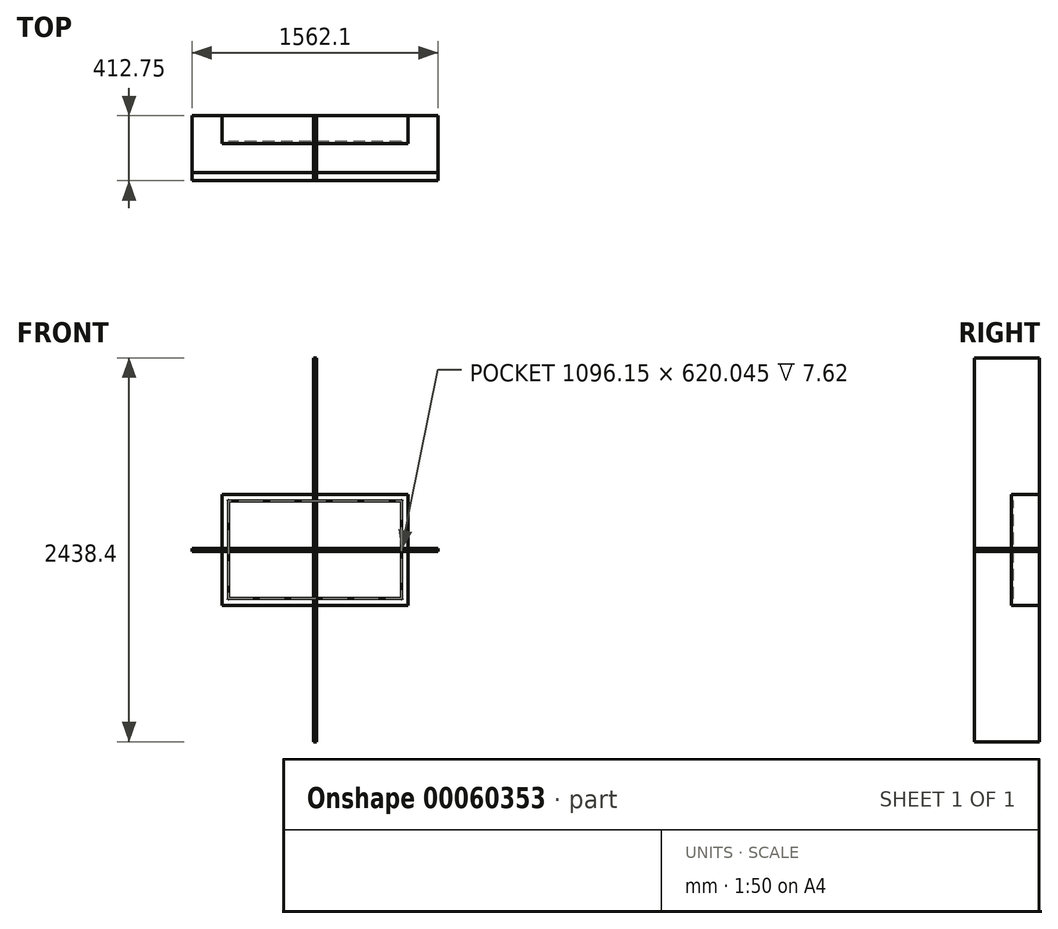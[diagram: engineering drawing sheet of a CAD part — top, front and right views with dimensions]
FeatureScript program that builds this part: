
annotation { "Feature Type Name" : "Feature", "Feature Type Description" : "" }
export const myFeature = defineFeature(function(context is Context, id is Id, definition is map)
    precondition{}
    {
        {
            var Q0;
            Q0=qCreatedBy(makeId("Front.planeOp"),FACE);
            var sketch = newSketch(context, id + "F0", { "sketchPlane" : qUnion([Q0])});
            skLineSegment(sketch, "E0.rect.bottom", {"start": v(590.55, 352.43) * mm, "end": v(-590.55, 352.43) * mm});
            skLineSegment(sketch, "E0.rect.top", {"start": v(590.55, -352.43) * mm, "end": v(-590.55, -352.43) * mm});
            skLineSegment(sketch, "E0.rect.left", {"start": v(590.55, 352.43) * mm, "end": v(590.55, -352.43) * mm});
            skLineSegment(sketch, "E0.rect.right", {"start": v(-590.55, 352.43) * mm, "end": v(-590.55, -352.43) * mm});
            skPoint(sketch, "E0.rect.middle", {"position": v(0, 0) * mm});
            skSolve(sketch);
        }
        {
            var Q0;
            Q0=makeQuery(id+"F0.imprint","IMPRINT",FACE,{"disambiguationData":[TD([[makeQuery(id+"F0.imprint","IMPRINT",EDGE,{"derivedFrom":sQuery(id+"F0.wireOp",EDGE,"E0.rect.bottom")}),1.0]])]});
            extrude(context, id + "F1", {"entities" : qUnion([Q0]), "depth" : 177.8 * mm});
        }
        {
            var Q0;
            Q0=makeQuery(id+"F1.opExtrude","CAP_FACE",FACE,{"disambiguationData":[OSD([sQuery(id+"F0.wireOp",EDGE,"E0.rect.bottom"),sQuery(id+"F0.wireOp",EDGE,"E0.rect.top"),sQuery(id+"F0.wireOp",EDGE,"E0.rect.left"),sQuery(id+"F0.wireOp",EDGE,"E0.rect.right")])],"isStart":false});
            var sketch = newSketch(context, id + "F2", { "sketchPlane" : qUnion([Q0])});
            skLineSegment(sketch, "E1.rect.bottom", {"start": v(548.08, -310.02) * mm, "end": v(-548.08, -310.02) * mm});
            skLineSegment(sketch, "E1.rect.top", {"start": v(548.08, 310.02) * mm, "end": v(-548.08, 310.02) * mm});
            skLineSegment(sketch, "E1.rect.left", {"start": v(548.08, -310.02) * mm, "end": v(548.08, 310.02) * mm});
            skLineSegment(sketch, "E1.rect.right", {"start": v(-548.08, -310.02) * mm, "end": v(-548.08, 310.02) * mm});
            skPoint(sketch, "E1.rect.middle", {"position": v(0, 0) * mm});
            skSolve(sketch);
        }
        {
            var Q0;
            Q0=qCreatedBy(makeId("Front.planeOp"),FACE);
            var sketch = newSketch(context, id + "F3", { "sketchPlane" : qUnion([Q0])});
            skLineSegment(sketch, "E2.rect.bottom", {"start": v(9.53, 1219.2) * mm, "end": v(-9.53, 1219.2) * mm});
            skLineSegment(sketch, "E2.rect.top", {"start": v(9.53, -1219.2) * mm, "end": v(-9.53, -1219.2) * mm});
            skLineSegment(sketch, "E2.rect.left", {"start": v(9.53, 1219.2) * mm, "end": v(9.53, -1219.2) * mm});
            skLineSegment(sketch, "E2.rect.right", {"start": v(-9.53, 1219.2) * mm, "end": v(-9.53, -1219.2) * mm});
            skPoint(sketch, "E2.rect.middle", {"position": v(0, 0) * mm});
            skSolve(sketch);
        }
        {
            var Q0;
            Q0=qCreatedBy(makeId("Front.planeOp"),FACE);
            var sketch = newSketch(context, id + "F4", { "sketchPlane" : qUnion([Q0])});
            skLineSegment(sketch, "E3.rect.bottom", {"start": v(781.05, 9.53) * mm, "end": v(-781.05, 9.53) * mm});
            skLineSegment(sketch, "E3.rect.top", {"start": v(781.05, -9.52) * mm, "end": v(-781.05, -9.52) * mm});
            skLineSegment(sketch, "E3.rect.left", {"start": v(781.05, 9.53) * mm, "end": v(781.05, -9.52) * mm});
            skLineSegment(sketch, "E3.rect.right", {"start": v(-781.05, 9.53) * mm, "end": v(-781.05, -9.52) * mm});
            skPoint(sketch, "E3.rect.middle", {"position": v(0, 0) * mm});
            skSolve(sketch);
        }
        {
            var Q0;
            Q0=makeQuery(id+"F4.imprint","IMPRINT",FACE,{"disambiguationData":[TD([[makeQuery(id+"F4.imprint","IMPRINT",EDGE,{"derivedFrom":sQuery(id+"F4.wireOp",EDGE,"E3.rect.bottom")}),1.0]])]});
            extrude(context, id + "F5", {"entities" : qUnion([Q0]), "depth" : 412.75 * mm});
        }
        {
            var Q0;
            Q0=makeQuery(id+"F4.imprint","IMPRINT",FACE,{"disambiguationData":[TD([[makeQuery(id+"F4.imprint","IMPRINT",EDGE,{"derivedFrom":sQuery(id+"F4.wireOp",EDGE,"E3.rect.bottom")}),1.0]])]});
            extrude(context, id + "F6", {"entities" : qUnion([Q0]), "depth" : 361.95 * mm});
        }
        {
            var Q0;
            Q0=makeQuery(id+"F4.imprint","IMPRINT",FACE,{"disambiguationData":[TD([[makeQuery(id+"F4.imprint","IMPRINT",EDGE,{"derivedFrom":sQuery(id+"F4.wireOp",EDGE,"E3.rect.bottom")}),1.0]])]});
            extrude(context, id + "F7", {"entities" : qUnion([Q0]), "depth" : 361.95 * mm});
        }
        {
            var Q0;
            Q0=makeQuery(id+"F4.imprint","IMPRINT",FACE,{"disambiguationData":[TD([[makeQuery(id+"F4.imprint","IMPRINT",EDGE,{"derivedFrom":sQuery(id+"F4.wireOp",EDGE,"E3.rect.bottom")}),1.0]])]});
            extrude(context, id + "F8", {"entities" : qUnion([Q0]), "depth" : 361.95 * mm});
        }
        {
            var Q0;
            Q0=makeQuery(id+"F4.imprint","IMPRINT",FACE,{"disambiguationData":[TD([[makeQuery(id+"F4.imprint","IMPRINT",EDGE,{"derivedFrom":sQuery(id+"F4.wireOp",EDGE,"E3.rect.bottom")}),1.0]])]});
            extrude(context, id + "F9", {"entities" : qUnion([Q0]), "depth" : 361.95 * mm});
        }
        {
            var Q0;
            Q0 = qSketchRegion(id + "F3", true);
            extrude(context, id + "F10", {"entities" : qUnion([Q0]), "depth" : 412.75 * mm});
        }
        {
            var Q0;
            Q0=makeQuery(id+"F2.imprint","IMPRINT",FACE,{"disambiguationData":[TD([[makeQuery(id+"F2.imprint","IMPRINT",EDGE,{"derivedFrom":sQuery(id+"F2.wireOp",EDGE,"E1.rect.bottom")}),-1.0]])]});
            extrude(context, id + "F11", {"entities" : qUnion([Q0]), "endBound" : BoundingType.SYMMETRIC, "oppositeDirection" : true, "depth" : 25.4 * mm});
        }
        {
            var Q0;
            Q0=makeQuery(id+"F11.opExtrude","SWEPT_BODY",BODY,{"disambiguationData":[OSD([sQuery(id+"F2.wireOp",EDGE,"E1.rect.bottom"),sQuery(id+"F2.wireOp",EDGE,"E1.rect.top"),sQuery(id+"F2.wireOp",EDGE,"E1.rect.left"),sQuery(id+"F2.wireOp",EDGE,"E1.rect.right")])]});
            var Q1;
            Q1=makeQuery(id+"F1.opExtrude","SWEPT_BODY",BODY,{"disambiguationData":[OSD([sQuery(id+"F0.wireOp",EDGE,"E0.rect.bottom"),sQuery(id+"F0.wireOp",EDGE,"E0.rect.top"),sQuery(id+"F0.wireOp",EDGE,"E0.rect.left"),sQuery(id+"F0.wireOp",EDGE,"E0.rect.right")])]});
            booleanBodies(context, id + "F12", {"operationType" : BooleanOperationType.SUBTRACTION, "tools" : qUnion([Q0]), "targets" : qUnion([Q1])});
        }
        {
            var Q0;
            Q0=makeQuery(id+"F12.opBoolean","INTERSECT",EDGE,{"derivedFrom":[makeQuery(id+"F1.opExtrude","CAP_FACE",FACE,{"disambiguationData":[OSD([sQuery(id+"F0.wireOp",EDGE,"E0.rect.bottom"),sQuery(id+"F0.wireOp",EDGE,"E0.rect.top"),sQuery(id+"F0.wireOp",EDGE,"E0.rect.left"),sQuery(id+"F0.wireOp",EDGE,"E0.rect.right")])],"isStart":false}),makeQuery(id+"F11.opExtrude","SWEPT_FACE",FACE,{"disambiguationData":[OSD([sQuery(id+"F2.wireOp",EDGE,"E1.rect.right")])]})]});
            var Q1;
            Q1=makeQuery(id+"F12.opBoolean","INTERSECT",EDGE,{"derivedFrom":[makeQuery(id+"F1.opExtrude","CAP_FACE",FACE,{"disambiguationData":[OSD([sQuery(id+"F0.wireOp",EDGE,"E0.rect.bottom"),sQuery(id+"F0.wireOp",EDGE,"E0.rect.top"),sQuery(id+"F0.wireOp",EDGE,"E0.rect.left"),sQuery(id+"F0.wireOp",EDGE,"E0.rect.right")])],"isStart":false}),makeQuery(id+"F11.opExtrude","SWEPT_FACE",FACE,{"disambiguationData":[OSD([sQuery(id+"F2.wireOp",EDGE,"E1.rect.top")])]})]});
            var Q2;
            Q2=makeQuery(id+"F12.opBoolean","INTERSECT",EDGE,{"derivedFrom":[makeQuery(id+"F1.opExtrude","CAP_FACE",FACE,{"disambiguationData":[OSD([sQuery(id+"F0.wireOp",EDGE,"E0.rect.bottom"),sQuery(id+"F0.wireOp",EDGE,"E0.rect.top"),sQuery(id+"F0.wireOp",EDGE,"E0.rect.left"),sQuery(id+"F0.wireOp",EDGE,"E0.rect.right")])],"isStart":false}),makeQuery(id+"F11.opExtrude","SWEPT_FACE",FACE,{"disambiguationData":[OSD([sQuery(id+"F2.wireOp",EDGE,"E1.rect.left")])]})]});
            var Q3;
            Q3=makeQuery(id+"F12.opBoolean","INTERSECT",EDGE,{"derivedFrom":[makeQuery(id+"F1.opExtrude","CAP_FACE",FACE,{"disambiguationData":[OSD([sQuery(id+"F0.wireOp",EDGE,"E0.rect.bottom"),sQuery(id+"F0.wireOp",EDGE,"E0.rect.top"),sQuery(id+"F0.wireOp",EDGE,"E0.rect.left"),sQuery(id+"F0.wireOp",EDGE,"E0.rect.right")])],"isStart":false}),makeQuery(id+"F11.opExtrude","SWEPT_FACE",FACE,{"disambiguationData":[OSD([sQuery(id+"F2.wireOp",EDGE,"E1.rect.bottom")])]})]});
            fillet(context, id + "F13", {"entities" : qUnion([Q0, Q1, Q2, Q3]), "radius" : 5.08 * mm, "tangentPropagation" : true, "allowEdgeOverflow" : false});
        }
    });
